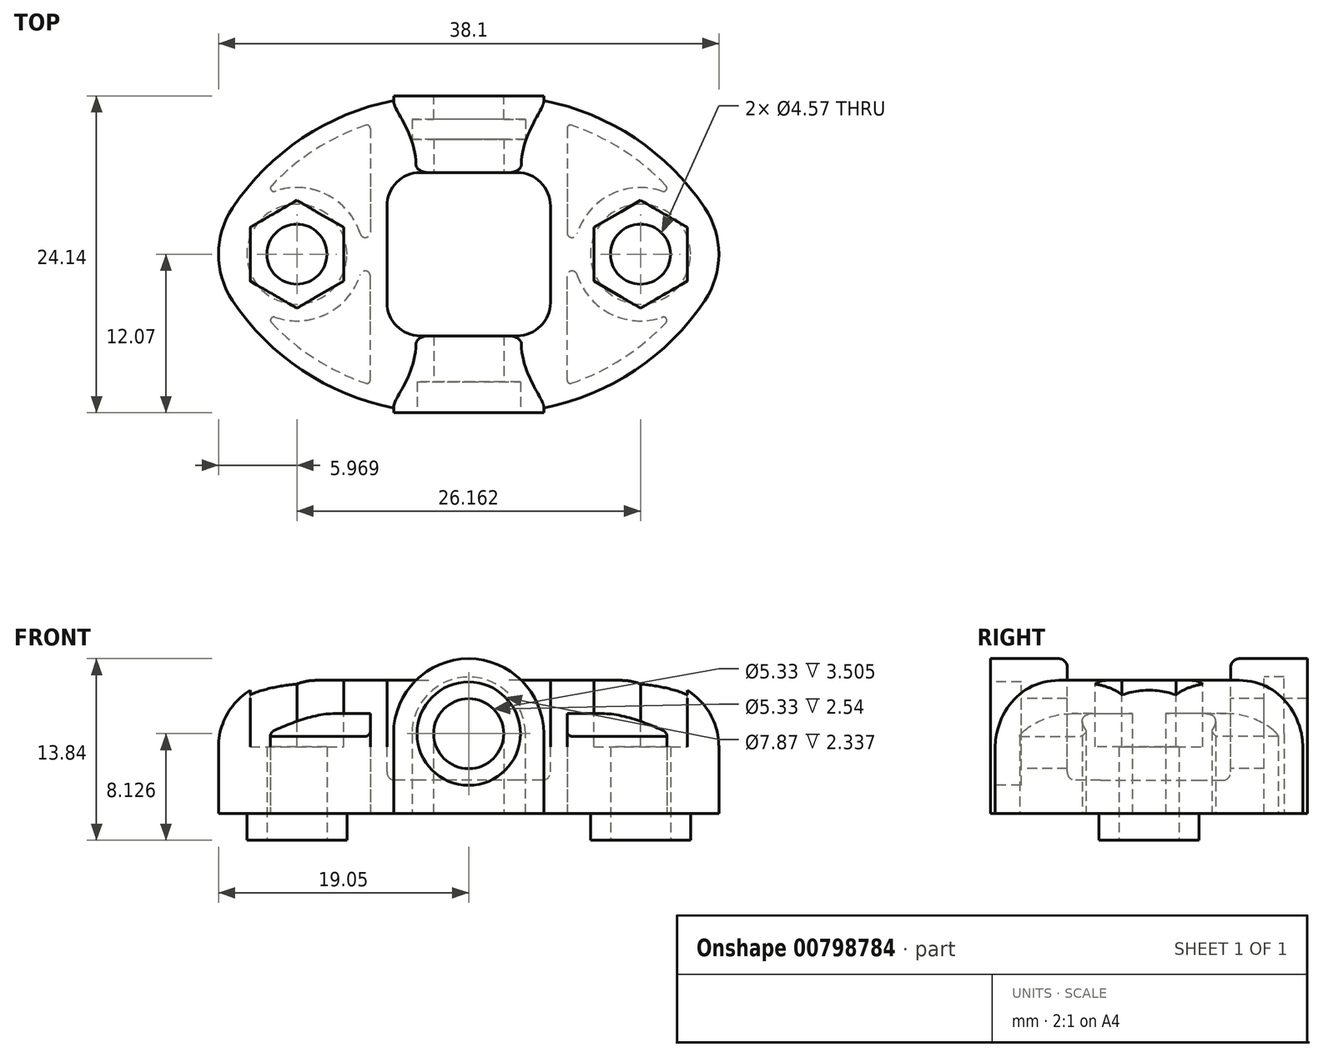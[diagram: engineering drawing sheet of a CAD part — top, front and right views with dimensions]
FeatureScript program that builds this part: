
annotation { "Feature Type Name" : "Feature", "Feature Type Description" : "" }
export const myFeature = defineFeature(function(context is Context, id is Id, definition is map)
    precondition{}
    {
        {
            var Q0;
            Q0=qCreatedBy(makeId("Top.planeOp"),FACE);
            var sketch = newSketch(context, id + "F0", { "sketchPlane" : qUnion([Q0])});
            skLineSegment(sketch, "E0.bottom", {"start": v(-19.05, 12.07) * mm, "end": v(19.05, 12.06) * mm, "construction": true});
            skLineSegment(sketch, "E0.top", {"start": v(-19.05, -12.06) * mm, "end": v(19.05, -12.07) * mm, "construction": true});
            skLineSegment(sketch, "E0.left", {"start": v(-19.05, 12.06) * mm, "end": v(-19.05, -12.06) * mm, "construction": true});
            skLineSegment(sketch, "E0.right", {"start": v(19.05, 12.06) * mm, "end": v(19.05, -12.06) * mm, "construction": true});
            skPoint(sketch, "E1.centerSnap0", {"position": v(-19.05, 0) * mm});
            skLineSegment(sketch, "E2", {"start": v(0, 12.07) * mm, "end": v(-2.03, 12.07) * mm});
            skLineSegment(sketch, "E3", {"start": v(0, -12.07) * mm, "end": v(-2.03, -12.07) * mm});
            skArc(sketch, "E4", {"start": v(-2.03, 12.07) * mm, "mid": v(-11.08, 9.8) * mm, "end": v(-17.99, 3.52) * mm});
            skArc(sketch, "E5.MirrorCS", {"start": v(-2.03, -12.07) * mm, "mid": v(-11.08, -9.8) * mm, "end": v(-17.99, -3.52) * mm});
            skArc(sketch, "E6", {"start": v(-17.99, 3.52) * mm, "mid": v(-19.05, 0) * mm, "end": v(-17.99, -3.52) * mm});
            skArc(sketch, "E7", {"start": v(-17.99, -3.52) * mm, "mid": v(-6.35, 0) * mm, "end": v(-17.99, 3.52) * mm, "construction": true});
            skLineSegment(sketch, "E8.MirrorCS", {"start": v(0, 12.07) * mm, "end": v(2.03, 12.07) * mm});
            skLineSegment(sketch, "E9.MirrorCS", {"start": v(0, -12.07) * mm, "end": v(2.03, -12.07) * mm});
            skArc(sketch, "E10.MirrorCS", {"start": v(2.03, 12.07) * mm, "mid": v(11.08, 9.8) * mm, "end": v(17.99, 3.52) * mm});
            skArc(sketch, "E11.MirrorCS", {"start": v(17.99, 3.52) * mm, "mid": v(19.05, 0) * mm, "end": v(17.99, -3.52) * mm});
            skArc(sketch, "E12.MirrorCS", {"start": v(2.03, -12.07) * mm, "mid": v(11.08, -9.8) * mm, "end": v(17.99, -3.52) * mm});
            skSolve(sketch);
        }
        {
            var Q0;
            Q0 = qSketchRegion(id + "F0", true);
            extrude(context, id + "F1", {"entities" : qUnion([Q0]), "depth" : 10.16 * mm, "offsetDistance" : 25.4 * mm});
        }
        {
            var Q0;
            Q0=makeQuery(id+"F1.opExtrude","CAP_FACE",FACE,{"disambiguationData":[OSD([sQuery(id+"F0.wireOp",EDGE,"E2"),sQuery(id+"F0.wireOp",EDGE,"E3"),sQuery(id+"F0.wireOp",EDGE,"E4"),sQuery(id+"F0.wireOp",EDGE,"E5.MirrorCS"),sQuery(id+"F0.wireOp",EDGE,"E6"),sQuery(id+"F0.wireOp",EDGE,"E8.MirrorCS"),sQuery(id+"F0.wireOp",EDGE,"E9.MirrorCS"),sQuery(id+"F0.wireOp",EDGE,"E10.MirrorCS"),sQuery(id+"F0.wireOp",EDGE,"E11.MirrorCS"),sQuery(id+"F0.wireOp",EDGE,"E12.MirrorCS")])],"isStart":false});
            fillet(context, id + "F2", {"entities" : qUnion([Q0]), "radius" : 5.08 * mm, "tangentPropagation" : true, "allowEdgeOverflow" : false});
        }
        {
            var Q0;
            Q0=makeQuery(id+"F1.opExtrude","CAP_FACE",FACE,{"disambiguationData":[OSD([sQuery(id+"F0.wireOp",EDGE,"E2"),sQuery(id+"F0.wireOp",EDGE,"E3"),sQuery(id+"F0.wireOp",EDGE,"E4"),sQuery(id+"F0.wireOp",EDGE,"E5.MirrorCS"),sQuery(id+"F0.wireOp",EDGE,"E6"),sQuery(id+"F0.wireOp",EDGE,"E8.MirrorCS"),sQuery(id+"F0.wireOp",EDGE,"E9.MirrorCS"),sQuery(id+"F0.wireOp",EDGE,"E10.MirrorCS"),sQuery(id+"F0.wireOp",EDGE,"E11.MirrorCS"),sQuery(id+"F0.wireOp",EDGE,"E12.MirrorCS")])],"isStart":false});
            var sketch = newSketch(context, id + "F3", { "sketchPlane" : qUnion([Q0])});
            skLineSegment(sketch, "E13.bottom", {"start": v(-3.68, 6.22) * mm, "end": v(3.68, 6.22) * mm});
            skLineSegment(sketch, "E13.top", {"start": v(-3.68, -6.22) * mm, "end": v(3.68, -6.22) * mm});
            skLineSegment(sketch, "E13.left", {"start": v(-6.22, 3.68) * mm, "end": v(-6.22, -3.68) * mm});
            skLineSegment(sketch, "E13.right", {"start": v(6.22, 3.68) * mm, "end": v(6.22, -3.68) * mm});
            skPoint(sketch, "E14.visualSharp", {"position": v(-6.22, 6.22) * mm});
            skArc(sketch, "E14.filletArc", {"start": v(-3.68, 6.22) * mm, "mid": v(-5.48, 5.48) * mm, "end": v(-6.22, 3.68) * mm});
            skPoint(sketch, "E15.visualSharp", {"position": v(6.22, 6.22) * mm});
            skArc(sketch, "E15.filletArc", {"start": v(6.22, 3.68) * mm, "mid": v(5.48, 5.48) * mm, "end": v(3.68, 6.22) * mm});
            skPoint(sketch, "E16.visualSharp", {"position": v(6.22, -6.22) * mm});
            skArc(sketch, "E16.filletArc", {"start": v(3.68, -6.22) * mm, "mid": v(5.48, -5.48) * mm, "end": v(6.22, -3.68) * mm});
            skPoint(sketch, "E17.visualSharp", {"position": v(-6.22, -6.22) * mm});
            skArc(sketch, "E17.filletArc", {"start": v(-6.22, -3.68) * mm, "mid": v(-5.48, -5.48) * mm, "end": v(-3.68, -6.22) * mm});
            skSolve(sketch);
        }
        {
            var Q0;
            Q0=qCreatedBy(makeId("Front.planeOp"),FACE);
            var sketch = newSketch(context, id + "F4", { "sketchPlane" : qUnion([Q0])});
            skLineSegment(sketch, "E18", {"start": v(-5.72, 6.1) * mm, "end": v(-5.71, 0) * mm});
            skLineSegment(sketch, "E19", {"start": v(-5.71, 0) * mm, "end": v(5.72, 0) * mm});
            skLineSegment(sketch, "E20", {"start": v(5.72, 0) * mm, "end": v(5.72, 6.1) * mm});
            skArc(sketch, "E21", {"start": v(-5.72, 6.1) * mm, "mid": v(0, 0.38) * mm, "end": v(5.72, 6.1) * mm, "construction": true});
            skArc(sketch, "E22", {"start": v(5.72, 6.1) * mm, "mid": v(0, 11.81) * mm, "end": v(-5.72, 6.1) * mm});
            skSolve(sketch);
        }
        {
            var Q0;
            Q0 = qSketchRegion(id + "F4", true);
            extrude(context, id + "F5", {"entities" : qUnion([Q0]), "operationType" : NewBodyOperationType.ADD, "endBound" : BoundingType.SYMMETRIC, "depth" : 24.13 * mm, "offsetDistance" : 25.4 * mm});
        }
        {
            var Q0;
            Q0 = qSketchRegion(id + "F3", true);
            extrude(context, id + "F6", {"entities" : qUnion([Q0]), "operationType" : NewBodyOperationType.REMOVE, "endBound" : BoundingType.UP_TO_NEXT, "oppositeDirection" : true, "depth" : 25.4 * mm, "hasOffset" : true, "offsetDistance" : 2.54 * mm});
        }
        {
            var Q0;
            Q0 = qSketchRegion(id + "F3", true);
            extrude(context, id + "F7", {"entities" : qUnion([Q0]), "operationType" : NewBodyOperationType.REMOVE, "endBound" : BoundingType.THROUGH_ALL, "depth" : 25.4 * mm, "offsetDistance" : 25.4 * mm});
        }
        {
            var Q0;
            {var subQ0=sQuery(id+"F3.wireOp",EDGE,"E14.filletArc");Q0=makeQuery(id+"F6.boolean.opBoolean","COPY",EDGE,{"disambiguationData":[topologyDisambiguationEdgeConnected([makeQuery(id+"F1.opExtrude","CAP_FACE",FACE,{"disambiguationData":[OSD([sQuery(id+"F0.wireOp",EDGE,"E2"),sQuery(id+"F0.wireOp",EDGE,"E3"),sQuery(id+"F0.wireOp",EDGE,"E4"),sQuery(id+"F0.wireOp",EDGE,"E5.MirrorCS"),sQuery(id+"F0.wireOp",EDGE,"E6"),sQuery(id+"F0.wireOp",EDGE,"E8.MirrorCS"),sQuery(id+"F0.wireOp",EDGE,"E9.MirrorCS"),sQuery(id+"F0.wireOp",EDGE,"E10.MirrorCS"),sQuery(id+"F0.wireOp",EDGE,"E11.MirrorCS"),sQuery(id+"F0.wireOp",EDGE,"E12.MirrorCS")])],"isStart":false})])],"derivedFrom":makeQuery(id+"F6.opExtrude","CAP_EDGE",EDGE,{"disambiguationData":[OSD([subQ0])],"isStart":true})});}
            var Q1;
            Q1=makeQuery(id+"F6.boolean.opBoolean","COPY",FACE,{"derivedFrom":makeQuery(id+"F6.opExtrude","CAP_FACE",FACE,{"disambiguationData":[OSD([sQuery(id+"F3.wireOp",EDGE,"E13.bottom"),sQuery(id+"F3.wireOp",EDGE,"E13.top"),sQuery(id+"F3.wireOp",EDGE,"E13.left"),sQuery(id+"F3.wireOp",EDGE,"E13.right"),sQuery(id+"F3.wireOp",EDGE,"E14.filletArc"),sQuery(id+"F3.wireOp",EDGE,"E15.filletArc"),sQuery(id+"F3.wireOp",EDGE,"E16.filletArc"),sQuery(id+"F3.wireOp",EDGE,"E17.filletArc")])],"isStart":false})});
            var Q2;
            Q2=makeQuery(id+"F6.boolean.opBoolean","COPY",EDGE,{"derivedFrom":makeQuery(id+"F6.opExtrude","CAP_EDGE",EDGE,{"disambiguationData":[OSD([sQuery(id+"F3.wireOp",EDGE,"E13.right")])],"isStart":true})});
            var Q3;
            Q3=makeQuery(id+"F7.boolean.opBoolean","INTERSECT",EDGE,{"derivedFrom":[makeQuery(id+"F5.opExtrude","SWEPT_FACE",FACE,{"disambiguationData":[OSD([sQuery(id+"F4.wireOp",EDGE,"E22")])]}),makeQuery(id+"F7.opExtrude","SWEPT_FACE",FACE,{"disambiguationData":[OSD([sQuery(id+"F3.wireOp",EDGE,"E13.bottom")])]})]});
            var Q4;
            Q4=makeQuery(id+"F7.boolean.opBoolean","INTERSECT",EDGE,{"derivedFrom":[makeQuery(id+"F5.opExtrude","SWEPT_FACE",FACE,{"disambiguationData":[OSD([sQuery(id+"F4.wireOp",EDGE,"E22")])]}),makeQuery(id+"F7.opExtrude","SWEPT_FACE",FACE,{"disambiguationData":[OSD([sQuery(id+"F3.wireOp",EDGE,"E13.top")])]})]});
            fillet(context, id + "F8", {"entities" : qUnion([Q0, Q1, Q2, Q3, Q4]), "radius" : 0.64 * mm, "tangentPropagation" : true, "allowEdgeOverflow" : false});
        }
        {
            var Q0;
            Q0=qCreatedBy(makeId("Front.planeOp"),FACE);
            var sketch = newSketch(context, id + "F9", { "sketchPlane" : qUnion([Q0])});
            skCircle(sketch, "E23", {"center": v(0, 6.1) * mm, "radius": 2.67 * mm});
            skSolve(sketch);
        }
        {
            var Q0;
            Q0 = qSketchRegion(id + "F9", true);
            extrude(context, id + "F10", {"entities" : qUnion([Q0]), "operationType" : NewBodyOperationType.REMOVE, "endBound" : BoundingType.SYMMETRIC, "oppositeDirection" : true, "depth" : 25.4 * mm, "offsetDistance" : 25.4 * mm});
        }
        {
            var Q0;
            Q0=makeQuery(id+"F1.opExtrude","CAP_FACE",FACE,{"disambiguationData":[OSD([sQuery(id+"F0.wireOp",EDGE,"E2"),sQuery(id+"F0.wireOp",EDGE,"E3"),sQuery(id+"F0.wireOp",EDGE,"E4"),sQuery(id+"F0.wireOp",EDGE,"E5.MirrorCS"),sQuery(id+"F0.wireOp",EDGE,"E6"),sQuery(id+"F0.wireOp",EDGE,"E8.MirrorCS"),sQuery(id+"F0.wireOp",EDGE,"E9.MirrorCS"),sQuery(id+"F0.wireOp",EDGE,"E10.MirrorCS"),sQuery(id+"F0.wireOp",EDGE,"E11.MirrorCS"),sQuery(id+"F0.wireOp",EDGE,"E12.MirrorCS")])],"isStart":false});
            var sketch = newSketch(context, id + "F11", { "sketchPlane" : qUnion([Q0])});
            skLineSegment(sketch, "E24", {"start": v(-9.52, 2.05) * mm, "end": v(-9.52, -2.05) * mm});
            skLineSegment(sketch, "E25", {"start": v(-9.52, -2.05) * mm, "end": v(-13.08, -4.1) * mm});
            skLineSegment(sketch, "E26", {"start": v(-13.08, -4.1) * mm, "end": v(-16.64, -2.05) * mm});
            skLineSegment(sketch, "E27", {"start": v(-16.64, -2.05) * mm, "end": v(-16.64, 2.05) * mm});
            skLineSegment(sketch, "E28", {"start": v(-16.64, 2.05) * mm, "end": v(-13.08, 4.1) * mm});
            skLineSegment(sketch, "E29", {"start": v(-13.08, 4.1) * mm, "end": v(-9.52, 2.05) * mm});
            skLineSegment(sketch, "E30.MirrorCS", {"start": v(16.64, 2.05) * mm, "end": v(13.08, 4.1) * mm});
            skLineSegment(sketch, "E31.MirrorCS", {"start": v(9.52, 2.05) * mm, "end": v(9.52, -2.05) * mm});
            skLineSegment(sketch, "E32.MirrorCS", {"start": v(13.08, 4.1) * mm, "end": v(9.52, 2.05) * mm});
            skLineSegment(sketch, "E33.MirrorCS", {"start": v(9.52, -2.05) * mm, "end": v(13.08, -4.1) * mm});
            skLineSegment(sketch, "E34.MirrorCS", {"start": v(16.64, -2.05) * mm, "end": v(16.64, 2.05) * mm});
            skLineSegment(sketch, "E35.MirrorCS", {"start": v(13.08, -4.1) * mm, "end": v(16.64, -2.05) * mm});
            skSolve(sketch);
        }
        {
            var Q0;
            Q0 = qSketchRegion(id + "F11", true);
            var Q1;
            Q1=makeQuery(id+"F1.opExtrude","CAP_FACE",FACE,{"disambiguationData":[OSD([sQuery(id+"F0.wireOp",EDGE,"E2"),sQuery(id+"F0.wireOp",EDGE,"E3"),sQuery(id+"F0.wireOp",EDGE,"E4"),sQuery(id+"F0.wireOp",EDGE,"E5.MirrorCS"),sQuery(id+"F0.wireOp",EDGE,"E6"),sQuery(id+"F0.wireOp",EDGE,"E8.MirrorCS"),sQuery(id+"F0.wireOp",EDGE,"E9.MirrorCS"),sQuery(id+"F0.wireOp",EDGE,"E10.MirrorCS"),sQuery(id+"F0.wireOp",EDGE,"E11.MirrorCS"),sQuery(id+"F0.wireOp",EDGE,"E12.MirrorCS")])],"isStart":true});
            extrude(context, id + "F12", {"entities" : qUnion([Q0]), "operationType" : NewBodyOperationType.REMOVE, "endBound" : BoundingType.UP_TO_SURFACE, "oppositeDirection" : true, "depth" : 25.4 * mm, "endBoundEntityFace" : qUnion([Q1]), "hasOffset" : true, "offsetDistance" : 5.08 * mm});
        }
        {
            var Q0;
            Q0=qCreatedBy(makeId("Top.planeOp"),FACE);
            var sketch = newSketch(context, id + "F13", { "sketchPlane" : qUnion([Q0])});
            skCircle(sketch, "E36", {"center": v(-13.08, 0) * mm, "radius": 3.81 * mm});
            skLineSegment(sketch, "E37", {"start": v(-13.08, 4.1) * mm, "end": v(-13.08, -4.1) * mm, "construction": true});
            skCircle(sketch, "E38.MirrorC", {"center": v(13.08, 0) * mm, "radius": 3.81 * mm});
            skSolve(sketch);
        }
        {
            var Q0;
            Q0 = qSketchRegion(id + "F13", true);
            extrude(context, id + "F14", {"entities" : qUnion([Q0]), "operationType" : NewBodyOperationType.ADD, "oppositeDirection" : true, "depth" : 2.03 * mm, "offsetDistance" : 25.4 * mm});
        }
        {
            var Q0;
            Q0=makeQuery(id+"F14.opExtrude","CAP_FACE",FACE,{"disambiguationData":[OSD([sQuery(id+"F13.wireOp",EDGE,"E36")])],"isStart":false});
            var sketch = newSketch(context, id + "F15", { "sketchPlane" : qUnion([Q0])});
            skCircle(sketch, "E39", {"center": v(-13.08, 0) * mm, "radius": 2.29 * mm});
            skCircle(sketch, "E40.MirrorC", {"center": v(13.08, 0) * mm, "radius": 2.29 * mm});
            skSolve(sketch);
        }
        {
            var Q0;
            Q0 = qSketchRegion(id + "F15", true);
            extrude(context, id + "F16", {"entities" : qUnion([Q0]), "operationType" : NewBodyOperationType.REMOVE, "endBound" : BoundingType.SYMMETRIC, "oppositeDirection" : true, "depth" : 25.4 * mm, "offsetDistance" : 25.4 * mm});
        }
        {
            var Q0;
            Q0=makeQuery(id+"F5.boolean.opBoolean","MERGE",FACE,{"derivedFrom":[makeQuery(id+"F1.opExtrude","SWEPT_FACE",FACE,{"disambiguationData":[OSD([sQuery(id+"F0.wireOp",EDGE,"E3"),sQuery(id+"F0.wireOp",EDGE,"E9.MirrorCS")])]}),makeQuery(id+"F5.opExtrude","CAP_FACE",FACE,{"disambiguationData":[OSD([sQuery(id+"F4.wireOp",EDGE,"E18"),sQuery(id+"F4.wireOp",EDGE,"E19"),sQuery(id+"F4.wireOp",EDGE,"E20"),sQuery(id+"F4.wireOp",EDGE,"E22")])],"isStart":false})]});
            var sketch = newSketch(context, id + "F17", { "sketchPlane" : qUnion([Q0])});
            skCircle(sketch, "E41", {"center": v(0, 6.1) * mm, "radius": 3.94 * mm});
            skSolve(sketch);
        }
        {
            var Q0;
            Q0 = qSketchRegion(id + "F17", true);
            extrude(context, id + "F18", {"entities" : qUnion([Q0]), "operationType" : NewBodyOperationType.REMOVE, "oppositeDirection" : true, "depth" : 2.34 * mm, "offsetDistance" : 25.4 * mm});
        }
        {
            var Q0;
            Q0=makeQuery(id+"F5.boolean.opBoolean","MERGE",FACE,{"derivedFrom":[makeQuery(id+"F1.opExtrude","SWEPT_FACE",FACE,{"disambiguationData":[OSD([sQuery(id+"F0.wireOp",EDGE,"E3"),sQuery(id+"F0.wireOp",EDGE,"E9.MirrorCS")])]}),makeQuery(id+"F5.opExtrude","CAP_FACE",FACE,{"disambiguationData":[OSD([sQuery(id+"F4.wireOp",EDGE,"E18"),sQuery(id+"F4.wireOp",EDGE,"E19"),sQuery(id+"F4.wireOp",EDGE,"E20"),sQuery(id+"F4.wireOp",EDGE,"E22")])],"isStart":false})]});
            cPlane(context, id + "F19", {"entities" : qUnion([Q0]), "cplaneType" : CPlaneType.OFFSET, "offset" : 20.83 * mm, "oppositeDirection" : true, "width" : 152.4 * mm, "height" : 152.4 * mm});
        }
        {
            var Q0;
            Q0=qCreatedBy(id+"F19.planeOp",FACE);
            var sketch = newSketch(context, id + "F20", { "sketchPlane" : qUnion([Q0])});
            skLineSegment(sketch, "E42", {"start": v(-4.32, 6.1) * mm, "end": v(-4.32, 6.1) * mm});
            skLineSegment(sketch, "E43", {"start": v(-4.32, 0) * mm, "end": v(4.32, 0) * mm});
            skLineSegment(sketch, "E44", {"start": v(4.32, 0) * mm, "end": v(4.32, 6.1) * mm});
            skLineSegment(sketch, "E45", {"start": v(-4.32, 6.1) * mm, "end": v(-4.32, 0) * mm});
            skLineSegment(sketch, "E46", {"start": v(4.32, 6.1) * mm, "end": v(4.32, 6.1) * mm});
            skArc(sketch, "E47", {"start": v(-4.32, 6.1) * mm, "mid": v(0, 1.78) * mm, "end": v(4.32, 6.1) * mm, "construction": true});
            skArc(sketch, "E48", {"start": v(4.32, 6.1) * mm, "mid": v(0, 10.41) * mm, "end": v(-4.32, 6.1) * mm});
            skSolve(sketch);
        }
        {
            var Q0;
            Q0 = qSketchRegion(id + "F20", true);
            extrude(context, id + "F21", {"entities" : qUnion([Q0]), "operationType" : NewBodyOperationType.REMOVE, "oppositeDirection" : true, "depth" : 1.52 * mm, "offsetDistance" : 25.4 * mm});
        }
        {
            var Q0;
            Q0=makeQuery(id+"F5.boolean.opBoolean","MERGE",FACE,{"derivedFrom":[makeQuery(id+"F1.opExtrude","SWEPT_FACE",FACE,{"disambiguationData":[OSD([sQuery(id+"F0.wireOp",EDGE,"E2"),sQuery(id+"F0.wireOp",EDGE,"E8.MirrorCS")])]}),makeQuery(id+"F5.opExtrude","CAP_FACE",FACE,{"disambiguationData":[OSD([sQuery(id+"F4.wireOp",EDGE,"E18"),sQuery(id+"F4.wireOp",EDGE,"E19"),sQuery(id+"F4.wireOp",EDGE,"E20"),sQuery(id+"F4.wireOp",EDGE,"E22")])],"isStart":true})]});
            var sketch = newSketch(context, id + "F22", { "sketchPlane" : qUnion([Q0])});
            skLineSegment(sketch, "E49", {"start": v(-2.67, 6.1) * mm, "end": v(-2.67, 0) * mm});
            skLineSegment(sketch, "E50", {"start": v(-2.67, 0) * mm, "end": v(2.67, 0) * mm});
            skLineSegment(sketch, "E51", {"start": v(2.67, 0) * mm, "end": v(2.67, 6.1) * mm});
            skArc(sketch, "E52", {"start": v(-2.67, 6.1) * mm, "mid": v(0, 3.43) * mm, "end": v(2.67, 6.1) * mm, "construction": true});
            skArc(sketch, "E53", {"start": v(2.67, 6.1) * mm, "mid": v(0, 8.76) * mm, "end": v(-2.67, 6.1) * mm});
            skSolve(sketch);
        }
        {
            var Q0;
            Q0 = qSketchRegion(id + "F22", true);
            var Q1;
            Q1=makeQuery(id+"F21.boolean.opBoolean","COPY",FACE,{"derivedFrom":makeQuery(id+"F21.opExtrude","CAP_FACE",FACE,{"disambiguationData":[OSD([sQuery(id+"F20.wireOp",EDGE,"E43"),sQuery(id+"F20.wireOp",EDGE,"E44"),sQuery(id+"F20.wireOp",EDGE,"E45"),sQuery(id+"F20.wireOp",EDGE,"E48")])],"isStart":true})});
            extrude(context, id + "F23", {"entities" : qUnion([Q0]), "operationType" : NewBodyOperationType.REMOVE, "endBound" : BoundingType.UP_TO_SURFACE, "oppositeDirection" : true, "depth" : 25.4 * mm, "endBoundEntityFace" : qUnion([Q1]), "offsetDistance" : 25.4 * mm});
        }
        {
            var Q0;
            Q0=qCreatedBy(makeId("Top.planeOp"),FACE);
            var sketch = newSketch(context, id + "F24", { "sketchPlane" : qUnion([Q0])});
            skCircle(sketch, "E54", {"center": v(-2.03, 7.1) * mm, "radius": 17.9 * mm, "construction": true});
            skCircle(sketch, "E55", {"center": v(-13.08, 0) * mm, "radius": 5.08 * mm, "construction": true});
            skLineSegment(sketch, "E56", {"start": v(-8.16, -1.27) * mm, "end": v(0, -1.27) * mm, "construction": true});
            skLineSegment(sketch, "E57", {"start": v(-7.5, 0) * mm, "end": v(-7.5, -9.94) * mm, "construction": true});
            skArc(sketch, "E58", {"start": v(-7.5, -1.65) * mm, "mid": v(-7.82, -1.27) * mm, "end": v(-8.24, -1.54) * mm});
            skArc(sketch, "E59", {"start": v(-14.75, -4.8) * mm, "mid": v(-15.05, -4.9) * mm, "end": v(-15.02, -5.21) * mm});
            skArc(sketch, "E60", {"start": v(-14.75, -4.8) * mm, "mid": v(-10.8, -4.54) * mm, "end": v(-8.24, -1.54) * mm});
            skArc(sketch, "E61", {"start": v(-7.83, -9.83) * mm, "mid": v(-7.6, -9.8) * mm, "end": v(-7.5, -9.59) * mm});
            skArc(sketch, "E62", {"start": v(-15.02, -5.21) * mm, "mid": v(-11.7, -7.96) * mm, "end": v(-7.83, -9.83) * mm});
            skLineSegment(sketch, "E63", {"start": v(-7.5, -9.59) * mm, "end": v(-7.5, -1.65) * mm});
            skArc(sketch, "E64.MirrorCS", {"start": v(14.75, -4.8) * mm, "mid": v(15.05, -4.9) * mm, "end": v(15.02, -5.21) * mm});
            skArc(sketch, "E65.MirrorCS", {"start": v(7.5, -1.65) * mm, "mid": v(7.82, -1.27) * mm, "end": v(8.24, -1.54) * mm});
            skLineSegment(sketch, "E66.MirrorCS", {"start": v(7.5, -9.59) * mm, "end": v(7.5, -1.65) * mm});
            skArc(sketch, "E67.MirrorCS", {"start": v(14.75, -4.8) * mm, "mid": v(10.8, -4.54) * mm, "end": v(8.24, -1.54) * mm});
            skArc(sketch, "E68.MirrorCS", {"start": v(7.83, -9.83) * mm, "mid": v(7.6, -9.8) * mm, "end": v(7.5, -9.59) * mm});
            skArc(sketch, "E69.MirrorCS", {"start": v(15.02, -5.21) * mm, "mid": v(11.7, -7.96) * mm, "end": v(7.83, -9.83) * mm});
            skArc(sketch, "E70.MirrorCS", {"start": v(-14.75, 4.8) * mm, "mid": v(-15.05, 4.9) * mm, "end": v(-15.02, 5.21) * mm});
            skArc(sketch, "E71.MirrorCS", {"start": v(-7.5, 1.65) * mm, "mid": v(-7.82, 1.27) * mm, "end": v(-8.24, 1.54) * mm});
            skArc(sketch, "E72.MirrorCS", {"start": v(-7.83, 9.83) * mm, "mid": v(-7.6, 9.8) * mm, "end": v(-7.5, 9.59) * mm});
            skLineSegment(sketch, "E73.MirrorCS", {"start": v(-7.5, 9.59) * mm, "end": v(-7.5, 1.65) * mm});
            skArc(sketch, "E74.MirrorCS", {"start": v(-14.75, 4.8) * mm, "mid": v(-10.8, 4.54) * mm, "end": v(-8.24, 1.54) * mm});
            skArc(sketch, "E75.MirrorCS", {"start": v(-15.02, 5.21) * mm, "mid": v(-11.7, 7.96) * mm, "end": v(-7.83, 9.83) * mm});
            skArc(sketch, "E76.MirrorCS", {"start": v(14.75, 4.8) * mm, "mid": v(15.05, 4.9) * mm, "end": v(15.02, 5.21) * mm});
            skArc(sketch, "E77.MirrorCS", {"start": v(7.5, 1.65) * mm, "mid": v(7.82, 1.27) * mm, "end": v(8.24, 1.54) * mm});
            skArc(sketch, "E78.MirrorCS", {"start": v(7.83, 9.83) * mm, "mid": v(7.6, 9.8) * mm, "end": v(7.5, 9.59) * mm});
            skLineSegment(sketch, "E79.MirrorCS", {"start": v(7.5, 9.59) * mm, "end": v(7.5, 1.65) * mm});
            skArc(sketch, "E80.MirrorCS", {"start": v(14.75, 4.8) * mm, "mid": v(10.8, 4.54) * mm, "end": v(8.24, 1.54) * mm});
            skArc(sketch, "E81.MirrorCS", {"start": v(15.02, 5.21) * mm, "mid": v(11.7, 7.96) * mm, "end": v(7.83, 9.83) * mm});
            skSolve(sketch);
        }
        {
            var Q0;
            Q0 = qSketchRegion(id + "F24", true);
            extrude(context, id + "F25", {"entities" : qUnion([Q0]), "operationType" : NewBodyOperationType.REMOVE, "endBound" : BoundingType.UP_TO_NEXT, "depth" : 25.4 * mm, "hasOffset" : true, "offsetDistance" : 2.54 * mm});
        }
    });
